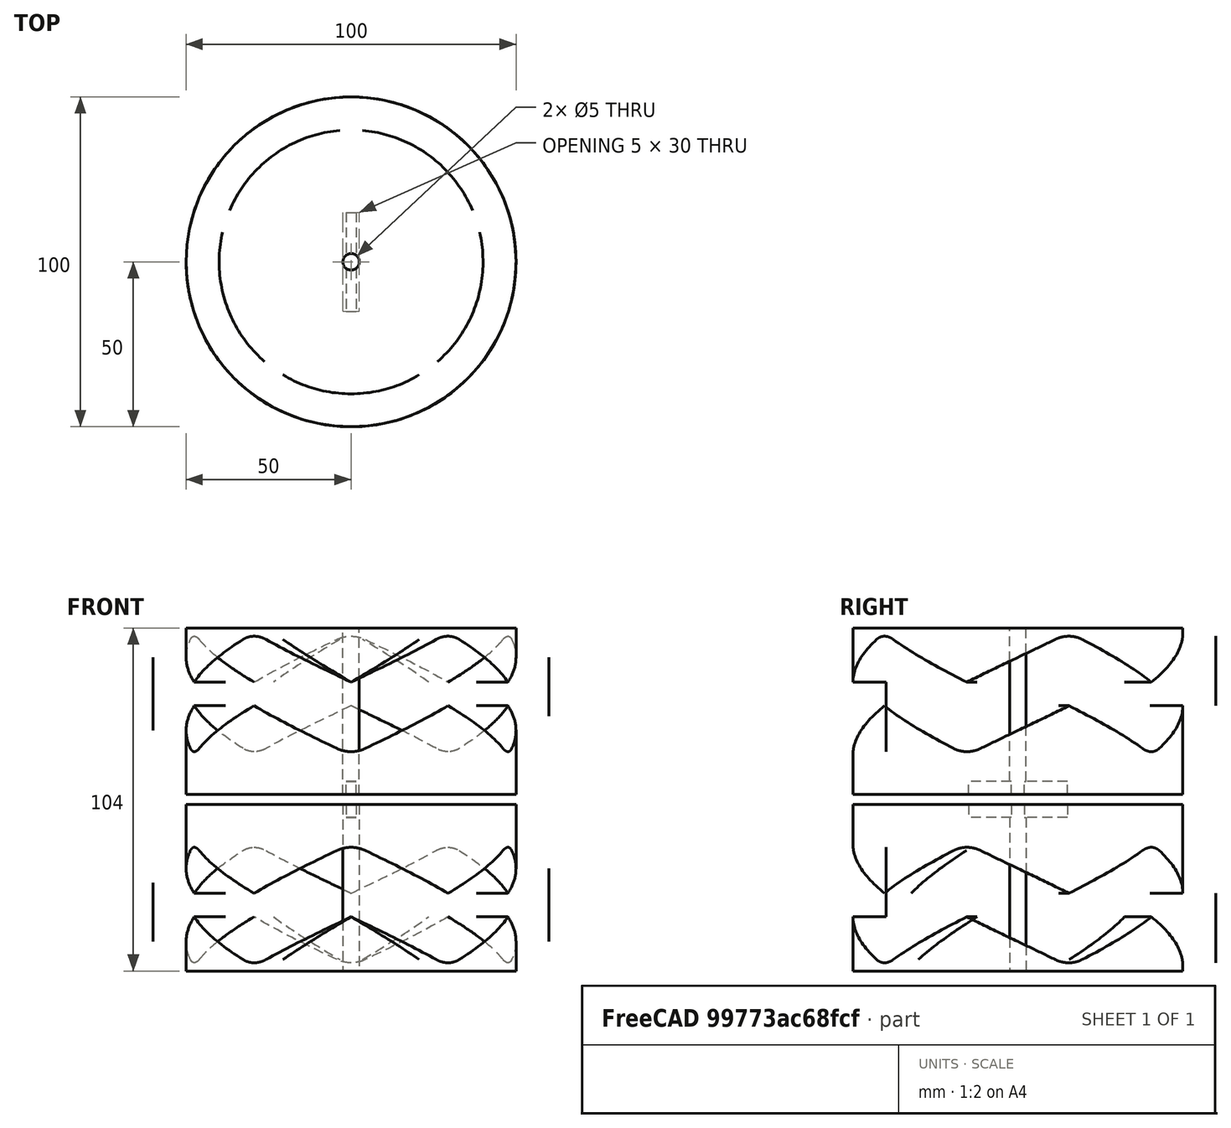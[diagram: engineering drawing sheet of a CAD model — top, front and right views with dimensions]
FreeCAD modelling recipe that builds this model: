
FCSTD DOCUMENT  (FreeCAD 0.22R38467 (Git))
Label: Rotor
objects: App::Link×2, App::VarSet×1, Part::MultiFuse×1, PartDesign::CoordinateSystem×1, App::Part×1
note: 2 computed .brp shape members not serialized (recipe doc carries the construction recipe); baked Part::Feature solids carry a one-line shape summary decoded from their .brp
EXTERNAL_REF file=camgroove.FCStd obj=Part

FEATURE [App::Link] Link  label="Top Cam"
  LinkPlacement = pos=(0,0,1.5) rot=(0,0,1;3.14159rad)
  LinkedObject = -> <external camgroove.FCStd>#Part
  Placement = pos=(0,0,1.5) rot=(0,0,1;3.14159rad)
FEATURE [App::Link] Link001  label="Bottom Cam"
  LinkPlacement = pos=(0,0,-1.5) rot=(1,0,0;3.14159rad)
  LinkedObject = -> <external camgroove.FCStd>#Part
  Placement = pos=(0,0,-1.5) rot=(1,0,0;3.14159rad)
FEATURE [App::VarSet] VarSet
  Height = 101
  expr: Height = <<Top Cam>>._shape.BoundBox.ZLength * 2 mm
FEATURE [Part::MultiFuse] Fusion
  Refine = true
  Shapes = -> [Link001,Link]
FEATURE [PartDesign::CoordinateSystem] LCS_Origin  label="Rotor Mid AP"
  AttacherType = Attacher::AttachEngine3D
  AttachmentOffset = pos=(0,0,-52) rot=(0,0,1;3.14159rad)
  AttachmentSupport = -> [Fusion]
  MapMode = 11
  Placement = pos=(0,0,0) rot=(0,0,1;1.5708rad)
  expr: .AttachmentOffset.Base.z = Fusion.Shape.BoundBox.ZLength * -0.5
FEATURE [App::Part] Rotor
  Group = -> [VarSet,LCS_Origin,Link,Link001,Fusion]
  Origin = -> Origin
